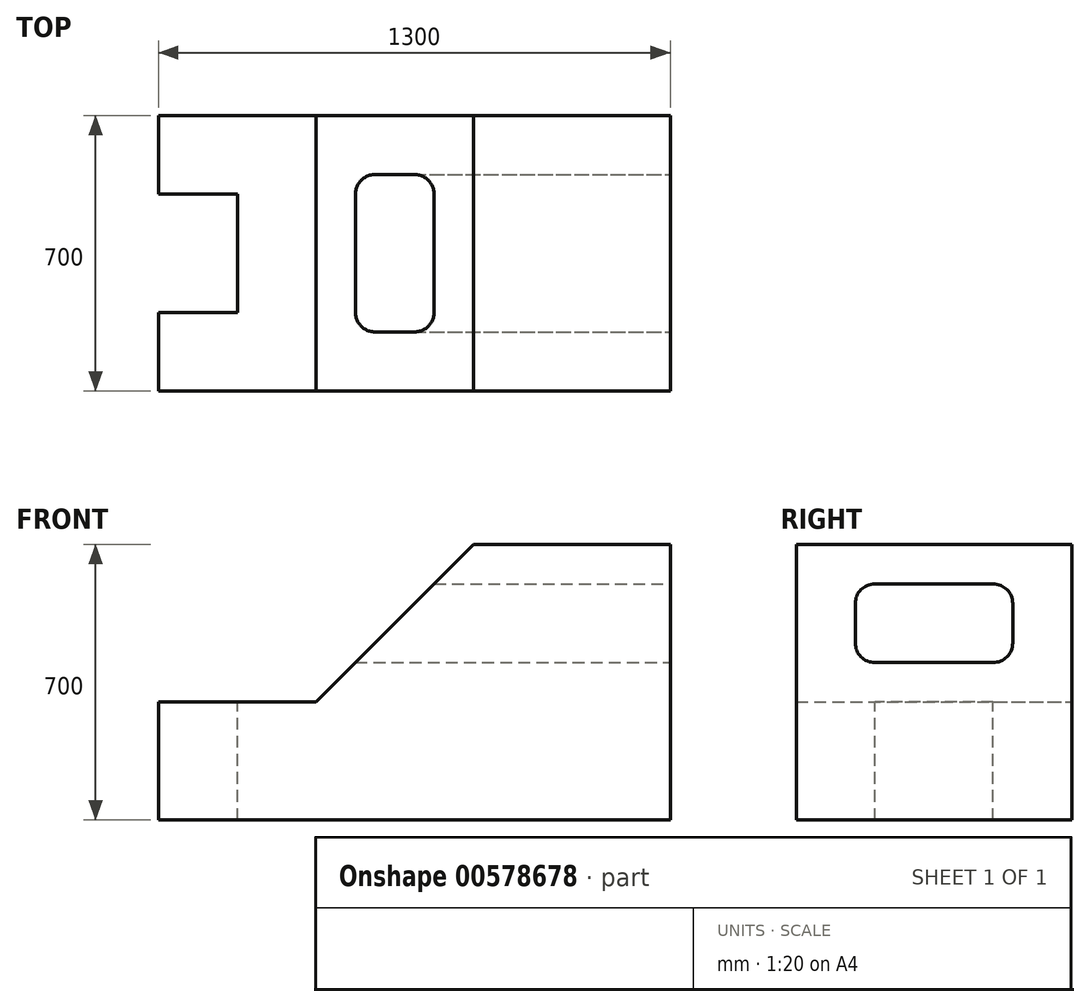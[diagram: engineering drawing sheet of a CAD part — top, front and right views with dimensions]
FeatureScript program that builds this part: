
annotation { "Feature Type Name" : "Feature", "Feature Type Description" : "" }
export const myFeature = defineFeature(function(context is Context, id is Id, definition is map)
    precondition{}
    {
        {
            var Q0;
            Q0=qCreatedBy(makeId("Front.planeOp"),FACE);
            var sketch = newSketch(context, id + "F0", { "sketchPlane" : qUnion([Q0])});
            skLineSegment(sketch, "E0.bottom", {"start": v(-650, -350) * mm, "end": v(650, -350) * mm});
            skLineSegment(sketch, "E0.top", {"start": v(150, 350) * mm, "end": v(650, 350) * mm});
            skLineSegment(sketch, "E0.left", {"start": v(-650, -350) * mm, "end": v(-650, -50) * mm});
            skLineSegment(sketch, "E0.right", {"start": v(650, -350) * mm, "end": v(650, 350) * mm});
            skPoint(sketch, "E0.middle", {"position": v(0, 0) * mm});
            skLineSegment(sketch, "E1", {"start": v(-650, -50) * mm, "end": v(-250, -50) * mm});
            skLineSegment(sketch, "E2", {"start": v(-250, -50) * mm, "end": v(150, 350) * mm});
            skPoint(sketch, "E3.orphan", {"position": v(-650, 350) * mm});
            skSolve(sketch);
        }
        {
            var Q0;
            Q0 = qSketchRegion(id + "F0", true);
            extrude(context, id + "F1", {"entities" : qUnion([Q0]), "depth" : 700 * mm, "offsetDistance" : 25.4 * mm});
        }
        {
            var Q0;
            Q0=makeQuery(id+"F1.opExtrude","SWEPT_FACE",FACE,{"disambiguationData":[OSD([sQuery(id+"F0.wireOp",EDGE,"E0.right")])]});
            var sketch = newSketch(context, id + "F2", { "sketchPlane" : qUnion([Q0])});
            skLineSegment(sketch, "E4", {"start": v(0, -350) * mm, "end": v(0, 50) * mm});
            skLineSegment(sketch, "E5", {"start": v(0, 50) * mm, "end": v(-150, 50) * mm});
            skLineSegment(sketch, "E6", {"start": v(-200, 50) * mm, "end": v(-500, 50) * mm});
            skLineSegment(sketch, "E7", {"start": v(-550, 50) * mm, "end": v(-700, 50) * mm});
            skLineSegment(sketch, "E8", {"start": v(-550, 100) * mm, "end": v(-550, 200) * mm});
            skLineSegment(sketch, "E9", {"start": v(-500, 250) * mm, "end": v(-200, 250) * mm});
            skLineSegment(sketch, "E10", {"start": v(-150, 200) * mm, "end": v(-150, 100) * mm});
            skPoint(sketch, "E11.visualSharp", {"position": v(-550, 250) * mm});
            skArc(sketch, "E11.filletArc", {"start": v(-500, 250) * mm, "mid": v(-535.36, 235.36) * mm, "end": v(-550, 200) * mm});
            skPoint(sketch, "E12.visualSharp", {"position": v(-150, 250) * mm});
            skArc(sketch, "E12.filletArc", {"start": v(-150, 200) * mm, "mid": v(-164.64, 235.36) * mm, "end": v(-200, 250) * mm});
            skPoint(sketch, "E13.visualSharp", {"position": v(-150, 50) * mm});
            skArc(sketch, "E13.filletArc", {"start": v(-200, 50) * mm, "mid": v(-164.64, 64.64) * mm, "end": v(-150, 100) * mm});
            skPoint(sketch, "E14.visualSharp", {"position": v(-550, 50) * mm});
            skArc(sketch, "E14.filletArc", {"start": v(-550, 100) * mm, "mid": v(-535.36, 64.64) * mm, "end": v(-500, 50) * mm});
            skSolve(sketch);
        }
        {
            var Q0;
            Q0 = qSketchRegion(id + "F2", true);
            extrude(context, id + "F3", {"entities" : qUnion([Q0]), "operationType" : NewBodyOperationType.REMOVE, "endBound" : BoundingType.THROUGH_ALL, "oppositeDirection" : true, "depth" : 25.4 * mm, "offsetDistance" : 25.4 * mm});
        }
        {
            var Q0;
            Q0=makeQuery(id+"F1.opExtrude","SWEPT_FACE",FACE,{"disambiguationData":[OSD([sQuery(id+"F0.wireOp",EDGE,"E1")])]});
            var sketch = newSketch(context, id + "F4", { "sketchPlane" : qUnion([Q0])});
            skLineSegment(sketch, "E15", {"start": v(-650, 0) * mm, "end": v(-650, -200) * mm});
            skLineSegment(sketch, "E16", {"start": v(-650, -200) * mm, "end": v(-650, -500) * mm});
            skLineSegment(sketch, "E17", {"start": v(-650, -500) * mm, "end": v(-650, -700) * mm});
            skLineSegment(sketch, "E18", {"start": v(-650, -200) * mm, "end": v(-450, -200) * mm});
            skLineSegment(sketch, "E19", {"start": v(-450, -200) * mm, "end": v(-450, -500) * mm});
            skLineSegment(sketch, "E20", {"start": v(-450, -500) * mm, "end": v(-650, -500) * mm});
            skSolve(sketch);
        }
        {
            var Q0;
            Q0 = qSketchRegion(id + "F4", true);
            extrude(context, id + "F5", {"entities" : qUnion([Q0]), "operationType" : NewBodyOperationType.ADD, "depth" : 25.4 * mm, "offsetDistance" : 25.4 * mm});
        }
        {
            var Q0;
            Q0=makeQuery(id+"F5.opExtrude","CAP_FACE",FACE,{"disambiguationData":[OSD([sQuery(id+"F4.wireOp",EDGE,"E16"),sQuery(id+"F4.wireOp",EDGE,"E18"),sQuery(id+"F4.wireOp",EDGE,"E19"),sQuery(id+"F4.wireOp",EDGE,"E20")])],"isStart":false});
            extrude(context, id + "F6", {"entities" : qUnion([Q0]), "operationType" : NewBodyOperationType.ADD, "depth" : 25.4 * mm, "offsetDistance" : 25.4 * mm});
        }
        {
            var Q0;
            Q0=makeQuery(id+"F6.opExtrude","CAP_FACE",FACE,{"disambiguationData":[OSD([sQuery(id+"F4.wireOp",EDGE,"E16"),sQuery(id+"F4.wireOp",EDGE,"E18"),sQuery(id+"F4.wireOp",EDGE,"E19"),sQuery(id+"F4.wireOp",EDGE,"E20")])],"isStart":false});
            extrude(context, id + "F7", {"entities" : qUnion([Q0]), "operationType" : NewBodyOperationType.REMOVE, "endBound" : BoundingType.THROUGH_ALL, "oppositeDirection" : true, "depth" : 25.4 * mm, "offsetDistance" : 25.4 * mm});
        }
    });
